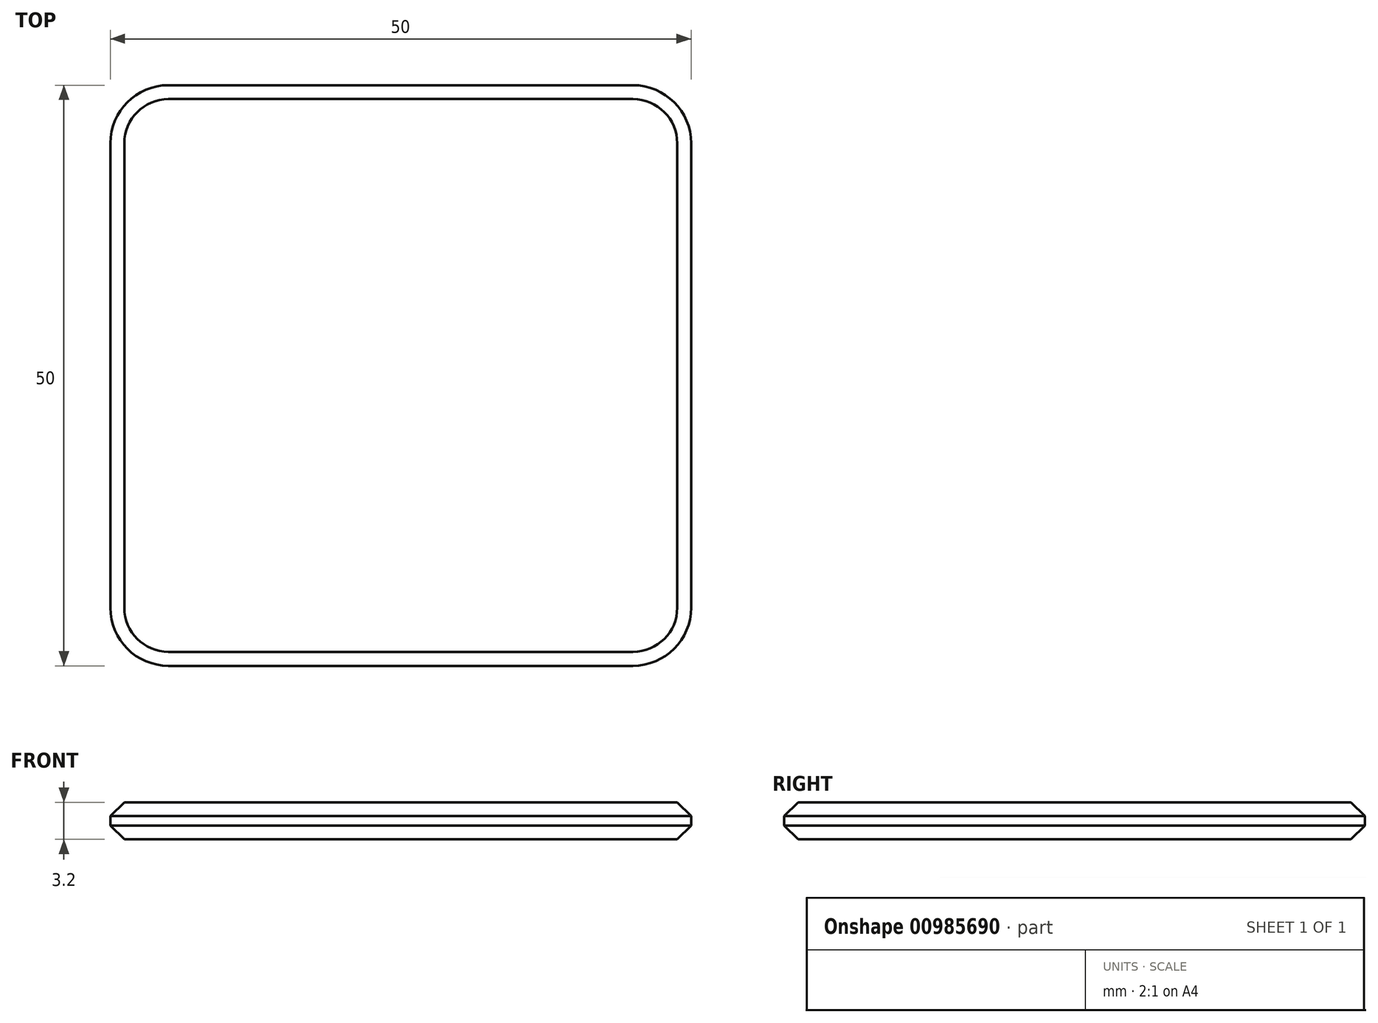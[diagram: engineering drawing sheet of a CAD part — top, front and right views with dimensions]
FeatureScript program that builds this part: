
annotation { "Feature Type Name" : "Feature", "Feature Type Description" : "" }
export const myFeature = defineFeature(function(context is Context, id is Id, definition is map)
    precondition{}
    {
        {
            var Q0;
            Q0=qCreatedBy(makeId("Top.planeOp"),FACE);
            var sketch = newSketch(context, id + "F0", { "sketchPlane" : qUnion([Q0])});
            skLineSegment(sketch, "E0.bottom", {"start": v(25, -25) * mm, "end": v(-25, -25) * mm});
            skLineSegment(sketch, "E0.top", {"start": v(25, 25) * mm, "end": v(-25, 25) * mm});
            skLineSegment(sketch, "E0.left", {"start": v(25, -25) * mm, "end": v(25, 25) * mm});
            skLineSegment(sketch, "E0.right", {"start": v(-25, -25) * mm, "end": v(-25, 25) * mm});
            skPoint(sketch, "E0.middle", {"position": v(0, 0) * mm});
            skSolve(sketch);
        }
        {
            var Q0;
            Q0=makeQuery(id+"F0.imprint","IMPRINT",FACE,{"disambiguationData":[TD([[makeQuery(id+"F0.imprint","IMPRINT",EDGE,{"derivedFrom":sQuery(id+"F0.wireOp",EDGE,"E0.bottom")}),-1.0]])]});
            extrude(context, id + "F1", {"entities" : qUnion([Q0]), "depth" : 3.2 * mm, "offsetDistance" : 25 * mm});
        }
        {
            var Q0;
            Q0=makeQuery(id+"F1.opExtrude","SWEPT_EDGE",EDGE,{"disambiguationData":[OSD([sQuery(id+"F0.wireOp",EDGE,"E0.bottom"),sQuery(id+"F0.wireOp",EDGE,"E0.right")])]});
            var Q1;
            Q1=makeQuery(id+"F1.opExtrude","SWEPT_EDGE",EDGE,{"disambiguationData":[OSD([sQuery(id+"F0.wireOp",EDGE,"E0.bottom"),sQuery(id+"F0.wireOp",EDGE,"E0.left")])]});
            var Q2;
            Q2=makeQuery(id+"F1.opExtrude","SWEPT_EDGE",EDGE,{"disambiguationData":[OSD([sQuery(id+"F0.wireOp",EDGE,"E0.top"),sQuery(id+"F0.wireOp",EDGE,"E0.left")])]});
            var Q3;
            Q3=makeQuery(id+"F1.opExtrude","SWEPT_EDGE",EDGE,{"disambiguationData":[OSD([sQuery(id+"F0.wireOp",EDGE,"E0.top"),sQuery(id+"F0.wireOp",EDGE,"E0.right")])]});
            fillet(context, id + "F2", {"entities" : qUnion([Q0, Q1, Q2, Q3]), "radius" : 5 * mm, "tangentPropagation" : true, "allowEdgeOverflow" : false});
        }
        {
            var Q0;
            Q0=makeQuery(id+"F1.opExtrude","CAP_FACE",FACE,{"disambiguationData":[OSD([sQuery(id+"F0.wireOp",EDGE,"E0.bottom"),sQuery(id+"F0.wireOp",EDGE,"E0.top"),sQuery(id+"F0.wireOp",EDGE,"E0.left"),sQuery(id+"F0.wireOp",EDGE,"E0.right")])],"isStart":true});
            var Q1;
            Q1=makeQuery(id+"F1.opExtrude","CAP_FACE",FACE,{"disambiguationData":[OSD([sQuery(id+"F0.wireOp",EDGE,"E0.bottom"),sQuery(id+"F0.wireOp",EDGE,"E0.top"),sQuery(id+"F0.wireOp",EDGE,"E0.left"),sQuery(id+"F0.wireOp",EDGE,"E0.right")])],"isStart":false});
            chamfer(context, id + "F3", {"entities" : qUnion([Q0, Q1]), "width" : 1.2 * mm, "tangentPropagation" : true});
        }
    });
